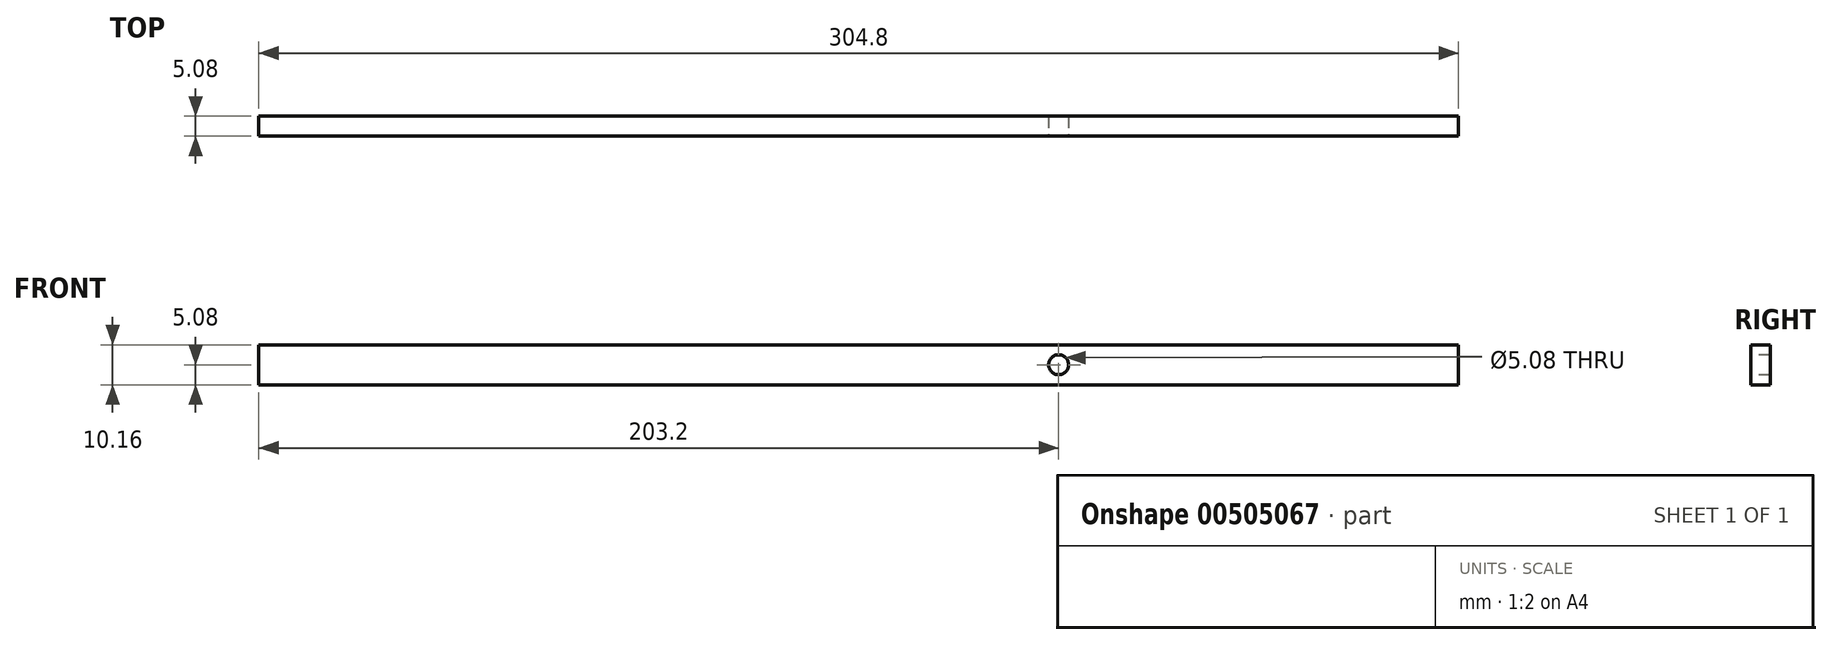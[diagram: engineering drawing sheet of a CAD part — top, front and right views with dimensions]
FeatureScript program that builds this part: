
annotation { "Feature Type Name" : "Feature", "Feature Type Description" : "" }
export const myFeature = defineFeature(function(context is Context, id is Id, definition is map)
    precondition{}
    {
        {
            var Q0;
            Q0=qCreatedBy(makeId("Front.planeOp"),FACE);
            var sketch = newSketch(context, id + "F0", { "sketchPlane" : qUnion([Q0])});
            skLineSegment(sketch, "E0.bottom", {"start": v(152.4, 0) * mm, "end": v(-152.4, 0) * mm});
            skLineSegment(sketch, "E0.top", {"start": v(152.4, 10.16) * mm, "end": v(-152.4, 10.16) * mm});
            skLineSegment(sketch, "E0.left", {"start": v(152.4, 0) * mm, "end": v(152.4, 10.16) * mm});
            skLineSegment(sketch, "E0.right", {"start": v(-152.4, 0) * mm, "end": v(-152.4, 10.16) * mm});
            skSolve(sketch);
        }
        {
            var Q0;
            Q0=makeQuery(id+"F0.imprint","IMPRINT",FACE,{"disambiguationData":[TD([[makeQuery(id+"F0.imprint","IMPRINT",EDGE,{"derivedFrom":sQuery(id+"F0.wireOp",EDGE,"E0.bottom")}),-1.0]])]});
            extrude(context, id + "F1", {"entities" : qUnion([Q0]), "depth" : 5.08 * mm});
        }
        {
            var Q0;
            Q0=makeQuery(id+"F1.opExtrude","CAP_FACE",FACE,{"disambiguationData":[OSD([sQuery(id+"F0.wireOp",EDGE,"E0.bottom"),sQuery(id+"F0.wireOp",EDGE,"E0.top"),sQuery(id+"F0.wireOp",EDGE,"E0.left"),sQuery(id+"F0.wireOp",EDGE,"E0.right")])],"isStart":false});
            var sketch = newSketch(context, id + "F2", { "sketchPlane" : qUnion([Q0])});
            skCircle(sketch, "E1", {"center": v(50.8, 5.08) * mm, "radius": 2.54 * mm});
            skSolve(sketch);
        }
        {
            var Q0;
            Q0=sQuery(id+"F2.wireOp",VERTEX,"E1.center");
            var Q1;
            Q1=makeQuery(id+"F1.opExtrude","SWEPT_BODY",BODY,{"disambiguationData":[OSD([sQuery(id+"F0.wireOp",EDGE,"E0.bottom"),sQuery(id+"F0.wireOp",EDGE,"E0.top"),sQuery(id+"F0.wireOp",EDGE,"E0.left"),sQuery(id+"F0.wireOp",EDGE,"E0.right")])]});
            hole(context, id + "F3", {"style" : HoleStyle.SIMPLE, "endStyle" : HoleEndStyle.THROUGH, "holeDiameter" : 5.08 * mm, "isTappedThrough" : true, "tappedDepth" : 12.7 * mm, "tapClearance" : 3, "locations" : qUnion([Q0]), "scope" : qUnion([Q1])});
        }
    });
